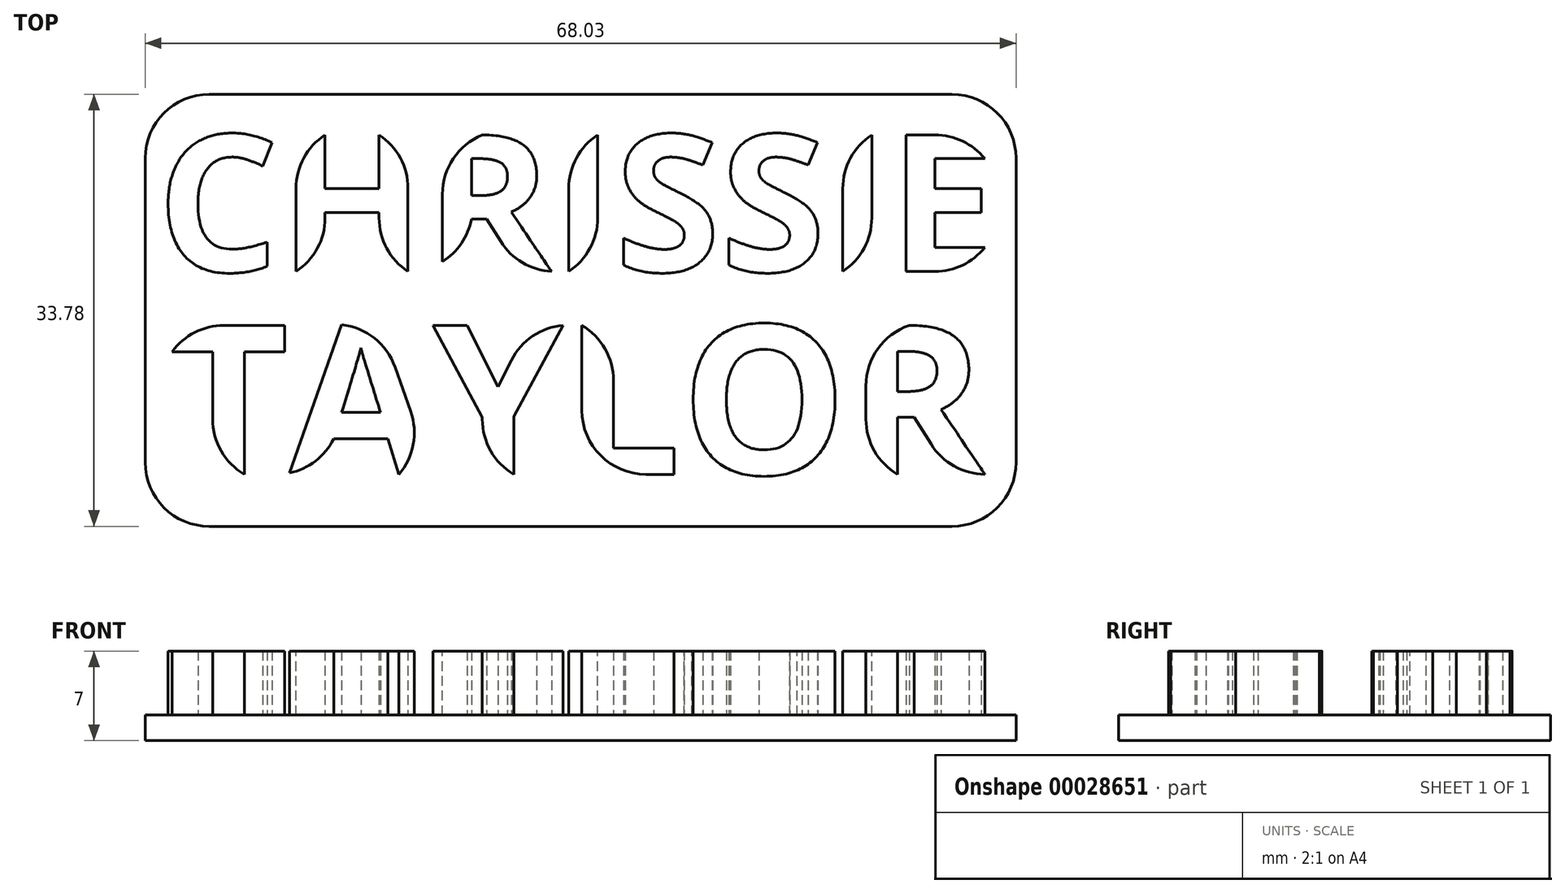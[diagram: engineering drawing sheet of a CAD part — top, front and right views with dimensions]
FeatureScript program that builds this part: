
annotation { "Feature Type Name" : "Feature", "Feature Type Description" : "" }
export const myFeature = defineFeature(function(context is Context, id is Id, definition is map)
    precondition{}
    {
        {
            var Q0;
            Q0=qCreatedBy(makeId("Top.planeOp"),FACE);
            var sketch = newSketch(context, id + "F0", { "sketchPlane" : qUnion([Q0])});
            skLineSegment(sketch, "E0.bottom", {"start": v(-30.85, 8.67) * mm, "end": v(37.18, 8.67) * mm});
            skLineSegment(sketch, "E0.top", {"start": v(-30.85, -25.1) * mm, "end": v(37.18, -25.1) * mm});
            skLineSegment(sketch, "E0.left", {"start": v(-30.85, 8.67) * mm, "end": v(-30.85, -25.1) * mm});
            skLineSegment(sketch, "E0.right", {"start": v(37.18, 8.67) * mm, "end": v(37.18, -25.1) * mm});
            skSolve(sketch);
        }
        {
            var Q0;
            Q0 = qSketchRegion(id + "F0", true);
            extrude(context, id + "F1", {"entities" : qUnion([Q0]), "depth" : 2 * mm});
        }
        {
            var Q0;
            Q0=makeQuery(id+"F1.opExtrude","CAP_FACE",FACE,{"disambiguationData":[OSD([sQuery(id+"F0.wireOp",EDGE,"E0.bottom"),sQuery(id+"F0.wireOp",EDGE,"E0.top"),sQuery(id+"F0.wireOp",EDGE,"E0.left"),sQuery(id+"F0.wireOp",EDGE,"E0.right")])],"isStart":false});
            var sketch = newSketch(context, id + "F2", { "sketchPlane" : qUnion([Q0])});
            skText(sketch, "E1", { "text": "CHRISSIE", "fontName": "OpenSans-Bold.ttf"});
            const initialGuessF2  = {"E1": [-0.02993, -0.00518, 1, 0, 0.01076]};
            skSetInitialGuess(sketch, initialGuessF2);
            skSolve(sketch);
        }
        {
            var Q0;
            Q0 = qSketchRegion(id + "F2", true);
            extrude(context, id + "F3", {"entities" : qUnion([Q0]), "operationType" : NewBodyOperationType.ADD, "depth" : 5 * mm});
        }
        {
            var Q0;
            Q0=makeQuery(id+"F1.opExtrude","SWEPT_EDGE",EDGE,{"disambiguationData":[OSD([sQuery(id+"F0.wireOp",EDGE,"E0.top"),sQuery(id+"F0.wireOp",EDGE,"E0.left")])]});
            var Q1;
            Q1=makeQuery(id+"F1.opExtrude","SWEPT_EDGE",EDGE,{"disambiguationData":[OSD([sQuery(id+"F0.wireOp",EDGE,"E0.bottom"),sQuery(id+"F0.wireOp",EDGE,"E0.left")])]});
            var Q2;
            Q2=makeQuery(id+"F1.opExtrude","SWEPT_EDGE",EDGE,{"disambiguationData":[OSD([sQuery(id+"F0.wireOp",EDGE,"E0.bottom"),sQuery(id+"F0.wireOp",EDGE,"E0.right")])]});
            var Q3;
            Q3=makeQuery(id+"F1.opExtrude","SWEPT_EDGE",EDGE,{"disambiguationData":[OSD([sQuery(id+"F0.wireOp",EDGE,"E0.top"),sQuery(id+"F0.wireOp",EDGE,"E0.right")])]});
            fillet(context, id + "F4", {"entities" : qUnion([Q0, Q1, Q2, Q3]), "radius" : 5 * mm, "tangentPropagation" : true, "allowEdgeOverflow" : false});
        }
        {
            var Q0;
            Q0=makeQuery(id+"F3.opExtrude","SWEPT_EDGE",EDGE,{"disambiguationData":[OSD([sQuery(id+"F2.wireOp",EDGE,"E1.sketch_text.stroke-18"),sQuery(id+"F2.wireOp",EDGE,"E1.sketch_text.stroke-19")])]});
            var Q1;
            Q1=makeQuery(id+"F3.opExtrude","SWEPT_EDGE",EDGE,{"disambiguationData":[OSD([sQuery(id+"F2.wireOp",EDGE,"E1.sketch_text.stroke-15"),sQuery(id+"F2.wireOp",EDGE,"E1.sketch_text.stroke-16")])]});
            var Q2;
            Q2=makeQuery(id+"F3.opExtrude","SWEPT_EDGE",EDGE,{"disambiguationData":[OSD([sQuery(id+"F2.wireOp",EDGE,"E1.sketch_text.stroke-34"),sQuery(id+"F2.wireOp",EDGE,"E1.sketch_text.stroke-35")])]});
            var Q3;
            Q3=makeQuery(id+"F3.opExtrude","SWEPT_EDGE",EDGE,{"disambiguationData":[OSD([sQuery(id+"F2.wireOp",EDGE,"E1.sketch_text.stroke-43"),sQuery(id+"F2.wireOp",EDGE,"E1.sketch_text.stroke-44")])]});
            var Q4;
            Q4=makeQuery(id+"F3.opExtrude","SWEPT_EDGE",EDGE,{"disambiguationData":[OSD([sQuery(id+"F2.wireOp",EDGE,"E1.sketch_text.stroke-48"),sQuery(id+"F2.wireOp",EDGE,"E1.sketch_text.stroke-49")])]});
            var Q5;
            Q5=makeQuery(id+"F3.opExtrude","SWEPT_EDGE",EDGE,{"disambiguationData":[OSD([sQuery(id+"F2.wireOp",EDGE,"E1.sketch_text.stroke-108"),sQuery(id+"F2.wireOp",EDGE,"E1.sketch_text.stroke-109")])]});
            var Q6;
            Q6=makeQuery(id+"F3.opExtrude","SWEPT_EDGE",EDGE,{"disambiguationData":[OSD([sQuery(id+"F2.wireOp",EDGE,"E1.sketch_text.stroke-110"),sQuery(id+"F2.wireOp",EDGE,"E1.sketch_text.stroke-121")])]});
            var Q7;
            Q7=makeQuery(id+"F3.opExtrude","SWEPT_EDGE",EDGE,{"disambiguationData":[OSD([sQuery(id+"F2.wireOp",EDGE,"E1.sketch_text.stroke-112"),sQuery(id+"F2.wireOp",EDGE,"E1.sketch_text.stroke-113")])]});
            var Q8;
            Q8=makeQuery(id+"F3.opExtrude","SWEPT_EDGE",EDGE,{"disambiguationData":[OSD([sQuery(id+"F2.wireOp",EDGE,"E1.sketch_text.stroke-25"),sQuery(id+"F2.wireOp",EDGE,"E1.sketch_text.stroke-26")])]});
            var Q9;
            Q9=makeQuery(id+"F3.opExtrude","SWEPT_EDGE",EDGE,{"disambiguationData":[OSD([sQuery(id+"F2.wireOp",EDGE,"E1.sketch_text.stroke-20"),sQuery(id+"F2.wireOp",EDGE,"E1.sketch_text.stroke-21")])]});
            var Q10;
            Q10=makeQuery(id+"F3.opExtrude","SWEPT_EDGE",EDGE,{"disambiguationData":[OSD([sQuery(id+"F2.wireOp",EDGE,"E1.sketch_text.stroke-36"),sQuery(id+"F2.wireOp",EDGE,"E1.sketch_text.stroke-37")])]});
            var Q11;
            Q11=makeQuery(id+"F3.opExtrude","SWEPT_EDGE",EDGE,{"disambiguationData":[OSD([sQuery(id+"F2.wireOp",EDGE,"E1.sketch_text.stroke-46"),sQuery(id+"F2.wireOp",EDGE,"E1.sketch_text.stroke-47")])]});
            var Q12;
            Q12=makeQuery(id+"F3.opExtrude","SWEPT_EDGE",EDGE,{"disambiguationData":[OSD([sQuery(id+"F2.wireOp",EDGE,"E1.sketch_text.stroke-106"),sQuery(id+"F2.wireOp",EDGE,"E1.sketch_text.stroke-107")])]});
            fillet(context, id + "F5", {"entities" : qUnion([Q0, Q1, Q2, Q3, Q4, Q5, Q6, Q7, Q8, Q9, Q10, Q11, Q12]), "radius" : 5 * mm, "tangentPropagation" : true, "allowEdgeOverflow" : false});
        }
        {
            var Q0;
            {var subQ0=sQuery(id+"F0.wireOp",EDGE,"E0.bottom");var subQ1=sQuery(id+"F0.wireOp",EDGE,"E0.top");var subQ2=sQuery(id+"F0.wireOp",EDGE,"E0.left");var subQ3=sQuery(id+"F0.wireOp",EDGE,"E0.right");Q0=makeQuery(id+"F3.boolean.opBoolean","SPLIT",FACE,{"disambiguationData":[TD([makeQuery(id+"F1.opExtrude","SWEPT_FACE",FACE,{"disambiguationData":[OSD([subQ0])]})])],"derivedFrom":makeQuery(id+"F1.opExtrude","CAP_FACE",FACE,{"disambiguationData":[OSD([subQ0,subQ1,subQ2,subQ3])],"isStart":false})});}
            var sketch = newSketch(context, id + "F6", { "sketchPlane" : qUnion([Q0])});
            skText(sketch, "E2", { "text": "TAYLOR", "fontName": "OpenSans-Bold.ttf"});
            const initialGuessF6  = {"E2": [-0.02907, -0.02104, 1, 0, 0.01174]};
            skSetInitialGuess(sketch, initialGuessF6);
            skSolve(sketch);
        }
        {
            var Q0;
            Q0 = qSketchRegion(id + "F6", true);
            extrude(context, id + "F7", {"entities" : qUnion([Q0]), "operationType" : NewBodyOperationType.ADD, "depth" : 5 * mm});
        }
        {
            var Q0;
            Q0=makeQuery(id+"F7.opExtrude","SWEPT_EDGE",EDGE,{"disambiguationData":[OSD([sQuery(id+"F6.wireOp",EDGE,"E2.sketch_text.stroke-0"),sQuery(id+"F6.wireOp",EDGE,"E2.sketch_text.stroke-1")])]});
            var Q1;
            Q1=makeQuery(id+"F7.opExtrude","SWEPT_EDGE",EDGE,{"disambiguationData":[OSD([sQuery(id+"F6.wireOp",EDGE,"E2.sketch_text.stroke-24"),sQuery(id+"F6.wireOp",EDGE,"E2.sketch_text.stroke-25")])]});
            var Q2;
            Q2=makeQuery(id+"F7.opExtrude","SWEPT_EDGE",EDGE,{"disambiguationData":[OSD([sQuery(id+"F6.wireOp",EDGE,"E2.sketch_text.stroke-29"),sQuery(id+"F6.wireOp",EDGE,"E2.sketch_text.stroke-34")])]});
            var Q3;
            Q3=makeQuery(id+"F7.opExtrude","SWEPT_EDGE",EDGE,{"disambiguationData":[OSD([sQuery(id+"F6.wireOp",EDGE,"E2.sketch_text.stroke-57"),sQuery(id+"F6.wireOp",EDGE,"E2.sketch_text.stroke-58")])]});
            var Q4;
            Q4=makeQuery(id+"F7.opExtrude","SWEPT_EDGE",EDGE,{"disambiguationData":[OSD([sQuery(id+"F6.wireOp",EDGE,"E2.sketch_text.stroke-65"),sQuery(id+"F6.wireOp",EDGE,"E2.sketch_text.stroke-66")])]});
            var Q5;
            Q5=makeQuery(id+"F7.opExtrude","SWEPT_EDGE",EDGE,{"disambiguationData":[OSD([sQuery(id+"F6.wireOp",EDGE,"E2.sketch_text.stroke-3"),sQuery(id+"F6.wireOp",EDGE,"E2.sketch_text.stroke-4")])]});
            var Q6;
            Q6=makeQuery(id+"F7.opExtrude","SWEPT_EDGE",EDGE,{"disambiguationData":[OSD([sQuery(id+"F6.wireOp",EDGE,"E2.sketch_text.stroke-13"),sQuery(id+"F6.wireOp",EDGE,"E2.sketch_text.stroke-14")])]});
            var Q7;
            Q7=makeQuery(id+"F7.opExtrude","SWEPT_EDGE",EDGE,{"disambiguationData":[OSD([sQuery(id+"F6.wireOp",EDGE,"E2.sketch_text.stroke-30"),sQuery(id+"F6.wireOp",EDGE,"E2.sketch_text.stroke-31")])]});
            var Q8;
            Q8=makeQuery(id+"F7.opExtrude","SWEPT_EDGE",EDGE,{"disambiguationData":[OSD([sQuery(id+"F6.wireOp",EDGE,"E2.sketch_text.stroke-58"),sQuery(id+"F6.wireOp",EDGE,"E2.sketch_text.stroke-59")])]});
            var Q9;
            Q9=makeQuery(id+"F7.opExtrude","SWEPT_EDGE",EDGE,{"disambiguationData":[OSD([sQuery(id+"F6.wireOp",EDGE,"E2.sketch_text.stroke-10"),sQuery(id+"F6.wireOp",EDGE,"E2.sketch_text.stroke-11")])]});
            var Q10;
            Q10=makeQuery(id+"F7.opExtrude","SWEPT_EDGE",EDGE,{"disambiguationData":[OSD([sQuery(id+"F6.wireOp",EDGE,"E2.sketch_text.stroke-14"),sQuery(id+"F6.wireOp",EDGE,"E2.sketch_text.stroke-15")])]});
            var Q11;
            Q11=makeQuery(id+"F7.opExtrude","SWEPT_EDGE",EDGE,{"disambiguationData":[OSD([sQuery(id+"F6.wireOp",EDGE,"E2.sketch_text.stroke-20"),sQuery(id+"F6.wireOp",EDGE,"E2.sketch_text.stroke-21")])]});
            fillet(context, id + "F8", {"entities" : qUnion([Q0, Q1, Q2, Q3, Q4, Q5, Q6, Q7, Q8, Q9, Q10, Q11]), "radius" : 5 * mm, "tangentPropagation" : true, "allowEdgeOverflow" : false});
        }
    });
